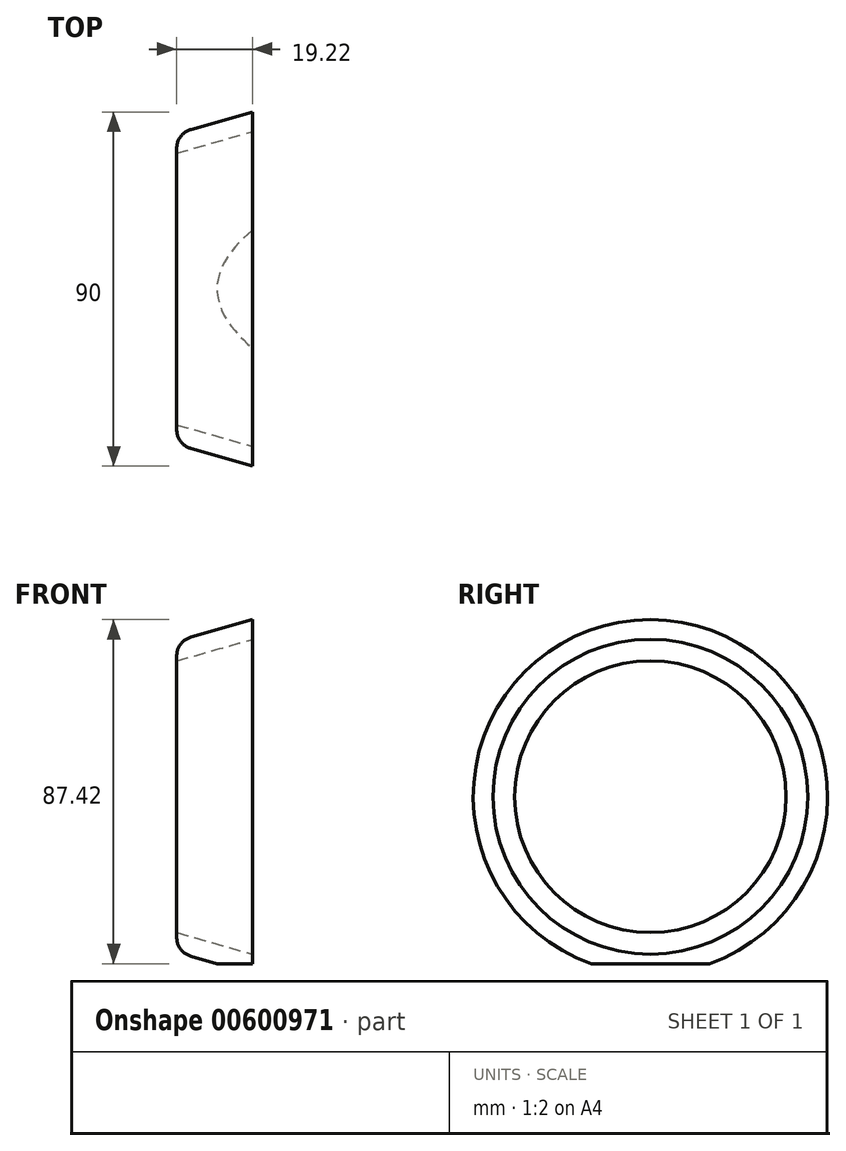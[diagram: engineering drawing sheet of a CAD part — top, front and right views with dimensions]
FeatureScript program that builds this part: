
annotation { "Feature Type Name" : "Feature", "Feature Type Description" : "" }
export const myFeature = defineFeature(function(context is Context, id is Id, definition is map)
    precondition{}
    {
        {
            var Q0;
            Q0=qCreatedBy(makeId("Front.planeOp"),FACE);
            var sketch = newSketch(context, id + "F0", { "sketchPlane" : qUnion([Q0])});
            skLineSegment(sketch, "E0.left", {"start": v(-52.48, 41.98) * mm, "end": v(-52.48, 7.48) * mm});
            skLineSegment(sketch, "E0.right", {"start": v(-33.26, 47.48) * mm, "end": v(-33.26, 7.48) * mm});
            skLineSegment(sketch, "E1", {"start": v(-52.48, 41.98) * mm, "end": v(-33.26, 47.48) * mm});
            skLineSegment(sketch, "E2", {"start": v(-52.48, 7.48) * mm, "end": v(-33.26, 7.48) * mm});
            skLineSegment(sketch, "E3", {"start": v(-33.26, 47.48) * mm, "end": v(-33.26, 52.48) * mm});
            skLineSegment(sketch, "E4", {"start": v(-52.48, 41.98) * mm, "end": v(-52.48, 46.98) * mm});
            skLineSegment(sketch, "E5", {"start": v(-52.48, 46.98) * mm, "end": v(-33.26, 52.48) * mm});
            skLineSegment(sketch, "E6.MirrorCS", {"start": v(-33.26, -32.52) * mm, "end": v(-33.26, 7.48) * mm});
            skLineSegment(sketch, "E7.MirrorCS", {"start": v(-52.48, -27.02) * mm, "end": v(-52.48, 7.48) * mm});
            skLineSegment(sketch, "E8.MirrorCS", {"start": v(-52.48, -27.02) * mm, "end": v(-33.26, -32.52) * mm});
            skLineSegment(sketch, "E9.MirrorCS", {"start": v(-52.48, -32.02) * mm, "end": v(-33.26, -37.52) * mm});
            skLineSegment(sketch, "E10.MirrorCS", {"start": v(-52.48, -27.02) * mm, "end": v(-52.48, -32.02) * mm});
            skLineSegment(sketch, "E11.MirrorCS", {"start": v(-33.26, -32.52) * mm, "end": v(-33.26, -37.52) * mm});
            skSolve(sketch);
        }
        {
            var Q0;
            Q0=makeQuery(id+"F0.imprint","IMPRINT",FACE,{"disambiguationData":[TD([[makeQuery(id+"F0.imprint","IMPRINT",EDGE,{"derivedFrom":sQuery(id+"F0.wireOp",EDGE,"E1")}),1.0]])]});
            var Q1;
            Q1=makeQuery(id+"F0.imprint","IMPRINT",FACE,{"disambiguationData":[TD([[makeQuery(id+"F0.imprint","IMPRINT",EDGE,{"derivedFrom":sQuery(id+"F0.wireOp",EDGE,"c2bfdc4a-e5b6-459e-925a-0be5c92ff4e80.MirrorCS")}),-1.0]])]});
            var Q2;
            {var subQ1=sQuery(id+"F0.wireOp",EDGE,"E3");Q2=makeQuery(id+"F0.imprint","IMPRINT",FACE,{"disambiguationData":[TD([[makeQuery(id+"F0.imprint","IMPRINT",EDGE,{"derivedFrom":subQ1}),-1.0]])]});}
            var Q3;
            Q3=sQuery(id+"F0.wireOp",EDGE,"E2");
            revolve(context, id + "F1", {"entities" : qUnion([Q0, Q1, Q2]), "axis" : qUnion([Q3]), "revolveType" : RevolveType.FULL});
        }
        {
            var Q0;
            Q0=qCreatedBy(makeId("Front.planeOp"),FACE);
            var sketch = newSketch(context, id + "F2", { "sketchPlane" : qUnion([Q0])});
            skLineSegment(sketch, "E12.bottom", {"start": v(-49.57, -47.9) * mm, "end": v(0.43, -47.9) * mm});
            skLineSegment(sketch, "E12.top", {"start": v(-49.57, -34.94) * mm, "end": v(0.43, -34.94) * mm});
            skLineSegment(sketch, "E12.left", {"start": v(-49.57, -47.9) * mm, "end": v(-49.57, -34.94) * mm});
            skLineSegment(sketch, "E12.right", {"start": v(0.43, -47.9) * mm, "end": v(0.43, -34.94) * mm});
            skSolve(sketch);
        }
        {
            var Q0;
            Q0=qSketchRegion(id+"F2",true);
            extrude(context, id + "F3", {"entities" : qUnion([Q0]), "operationType" : NewBodyOperationType.REMOVE, "endBound" : BoundingType.SYMMETRIC, "oppositeDirection" : true, "depth" : 70.2 * mm, "offsetDistance" : 25 * mm});
        }
        {
            var Q0;
            Q0=makeQuery(id+"F1.opRevolve","SWEPT_EDGE",EDGE,{"disambiguationData":[OSD([sQuery(id+"F0.wireOp",EDGE,"a673c032-d0a1-4c3f-9cd5-afd58c44c5de0.MirrorCS"),sQuery(id+"F0.wireOp",EDGE,"f61c0853-5b7b-4805-88cf-b8fb3abf6acf0.MirrorCS")])]});
            var Q1;
            Q1=makeQuery(id+"FhBYYEJiCrk1Cum_1.boolean.opBoolean","INTERSECT",EDGE,{"disambiguationData":[OD(1.0)],"derivedFrom":[makeQuery(id+"F1.opRevolve","SWEPT_FACE",FACE,{"disambiguationData":[OSD([sQuery(id+"F0.wireOp",EDGE,"KK8kL32Y-kdgn-8JmI-LohN-8wbJ6vsak4j2")])]}),makeQuery(id+"FhBYYEJiCrk1Cum_1.opExtrude","SWEPT_FACE",FACE,{"disambiguationData":[OSD([sQuery(id+"FIAtSWa8xYkcMIG_1.wireOp",EDGE,"ValE2jqm-DVIY-ARov-uIMi-ZkL4i5qOhdit.top")])]})]});
            var Q2;
            Q2=makeQuery(id+"FhBYYEJiCrk1Cum_1.boolean.opBoolean","INTERSECT",EDGE,{"disambiguationData":[OD(1.0)],"derivedFrom":[makeQuery(id+"F1.opRevolve","SWEPT_FACE",FACE,{"disambiguationData":[OSD([sQuery(id+"F0.wireOp",EDGE,"KK8kL32Y-kdgn-8JmI-LohN-8wbJ6vsak4j2")])]}),makeQuery(id+"FhBYYEJiCrk1Cum_1.opExtrude","SWEPT_FACE",FACE,{"disambiguationData":[OSD([sQuery(id+"FIAtSWa8xYkcMIG_1.wireOp",EDGE,"ValE2jqm-DVIY-ARov-uIMi-ZkL4i5qOhdit.bottom")])]})]});
            var Q3;
            Q3=makeQuery(id+"F1.opRevolve","SWEPT_EDGE",EDGE,{"disambiguationData":[OSD([sQuery(id+"F0.wireOp",EDGE,"E4"),sQuery(id+"F0.wireOp",EDGE,"E5")])]});
            fillet(context, id + "F4", {"entities" : qUnion([Q0, Q1, Q2, Q3]), "radius" : 5 * mm, "tangentPropagation" : true, "allowEdgeOverflow" : false});
        }
    });
